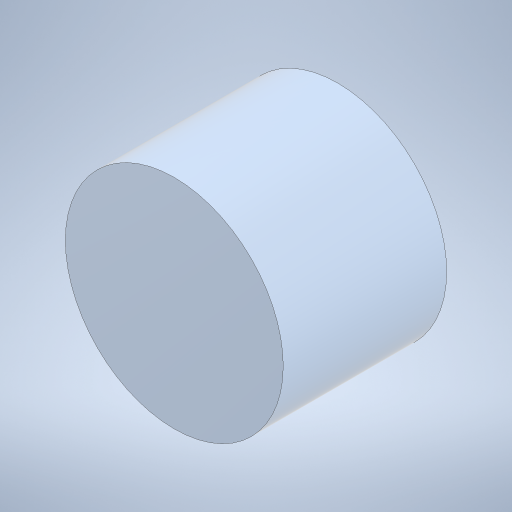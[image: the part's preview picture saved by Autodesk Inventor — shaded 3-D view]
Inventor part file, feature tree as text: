
AUTODESK INVENTOR PART (.ipt)
format: ipt  version: 2023 (Build 270158000, 158)  size: 227,840 bytes
history: native  units: in
note: dims shown in document units (in); Inventor stores cm internally (conversion verified against a paired STEP export)
features: sketch x2, extrude x1, hole x1, thread x1
ambient origin geometry x8: Origin, YZ Plane, XZ Plane, XY Plane, X Axis, Y Axis, Z Axis, Center Point
bodies: Solid1 (feature_tree)
feature tree (5):
  extrude  "Extrusion1"  Depth=0.5906in TaperAngle=0.0deg
  hole  "Hole1"  [1 undecoded]
  thread  "Thread1"  [1 undecoded]
  sketch  "Sketch1"  dims[d0=0.7874in d1=0.5906in d2=0.0in]
  sketch  "Sketch2"  dims[d3=0.1181in d4=0.75in d5=0.375in d6=0.25in d7=0.5635in d8=0.2362in d9=0.8108in d10=3.0in d11=0.0in d12=0.0625in d13=0.75in d14=0.375in]
note: 2 required parameter values undecoded (feature->parameter linkage not recoverable at this tier; creation-order binding heuristic only, values carry confidence <= 0.55)
